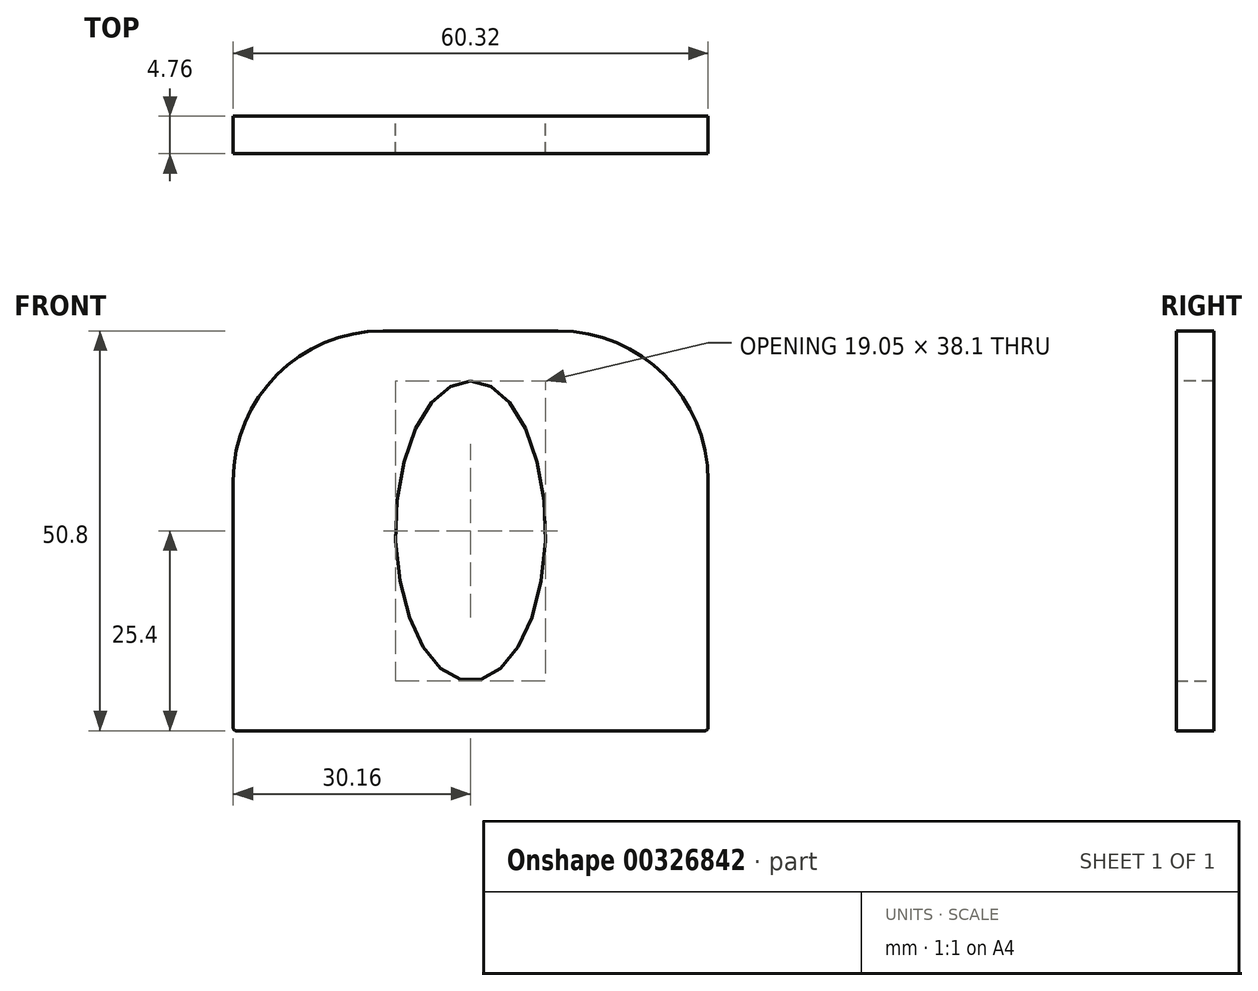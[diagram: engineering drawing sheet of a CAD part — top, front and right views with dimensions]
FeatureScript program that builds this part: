
annotation { "Feature Type Name" : "Feature", "Feature Type Description" : "" }
export const myFeature = defineFeature(function(context is Context, id is Id, definition is map)
    precondition{}
    {
        {
            var Q0;
            Q0=qCreatedBy(makeId("Front.planeOp"),FACE);
            var sketch = newSketch(context, id + "F0", { "sketchPlane" : qUnion([Q0])});
            skLineSegment(sketch, "E0.bottom", {"start": v(-30.16, 19.05) * mm, "end": v(30.16, 19.05) * mm});
            skLineSegment(sketch, "E0.top", {"start": v(-30.16, -31.75) * mm, "end": v(30.16, -31.75) * mm});
            skLineSegment(sketch, "E0.left", {"start": v(-30.16, 19.05) * mm, "end": v(-30.16, -31.75) * mm});
            skLineSegment(sketch, "E0.right", {"start": v(30.16, 19.05) * mm, "end": v(30.16, -31.75) * mm});
            skSolve(sketch);
        }
        {
            var Q0;
            Q0=qSketchRegion(id+"F0",true);
            extrude(context, id + "F1", {"entities" : qUnion([Q0]), "depth" : 4.76 * mm});
        }
        {
            var Q0;
            Q0=makeQuery(id+"F1.opExtrude","SWEPT_EDGE",EDGE,{"disambiguationData":[OSD([sQuery(id+"F0.wireOp",EDGE,"E0.bottom"),sQuery(id+"F0.wireOp",EDGE,"E0.left")])]});
            var Q1;
            Q1=makeQuery(id+"F1.opExtrude","SWEPT_EDGE",EDGE,{"disambiguationData":[OSD([sQuery(id+"F0.wireOp",EDGE,"E0.bottom"),sQuery(id+"F0.wireOp",EDGE,"E0.right")])]});
            fillet(context, id + "F2", {"entities" : qUnion([Q0, Q1]), "radius" : 19.05 * mm, "tangentPropagation" : true, "allowEdgeOverflow" : false});
        }
        {
            var Q0;
            Q0=makeQuery(id+"F1.opExtrude","SWEPT_EDGE",EDGE,{"disambiguationData":[OSD([sQuery(id+"F0.wireOp",EDGE,"E0.top"),sQuery(id+"F0.wireOp",EDGE,"E0.left")])]});
            var Q1;
            Q1=makeQuery(id+"F1.opExtrude","SWEPT_EDGE",EDGE,{"disambiguationData":[OSD([sQuery(id+"F0.wireOp",EDGE,"E0.top"),sQuery(id+"F0.wireOp",EDGE,"E0.right")])]});
            fillet(context, id + "F3", {"entities" : qUnion([Q0, Q1]), "radius" : 0.38 * mm, "tangentPropagation" : true, "allowEdgeOverflow" : false});
        }
        {
            var Q0;
            Q0=makeQuery(id+"F1.opExtrude","CAP_FACE",FACE,{"disambiguationData":[OSD([sQuery(id+"F0.wireOp",EDGE,"E0.bottom"),sQuery(id+"F0.wireOp",EDGE,"E0.top"),sQuery(id+"F0.wireOp",EDGE,"E0.left"),sQuery(id+"F0.wireOp",EDGE,"E0.right")])],"isStart":false});
            var sketch = newSketch(context, id + "F4", { "sketchPlane" : qUnion([Q0])});
            skEllipse(sketch, "E1.0", {"center": v(0, -6.35) * mm, "majorRadius": 19.05 * mm, "minorRadius": 9.53 * mm, "majorAxis": v(0, 1)});
            skSolve(sketch);
        }
        {
            var Q0;
            Q0=qSketchRegion(id+"F4",true);
            extrude(context, id + "F5", {"entities" : qUnion([Q0]), "operationType" : NewBodyOperationType.REMOVE, "oppositeDirection" : true, "depth" : 25.4 * mm});
        }
    });
